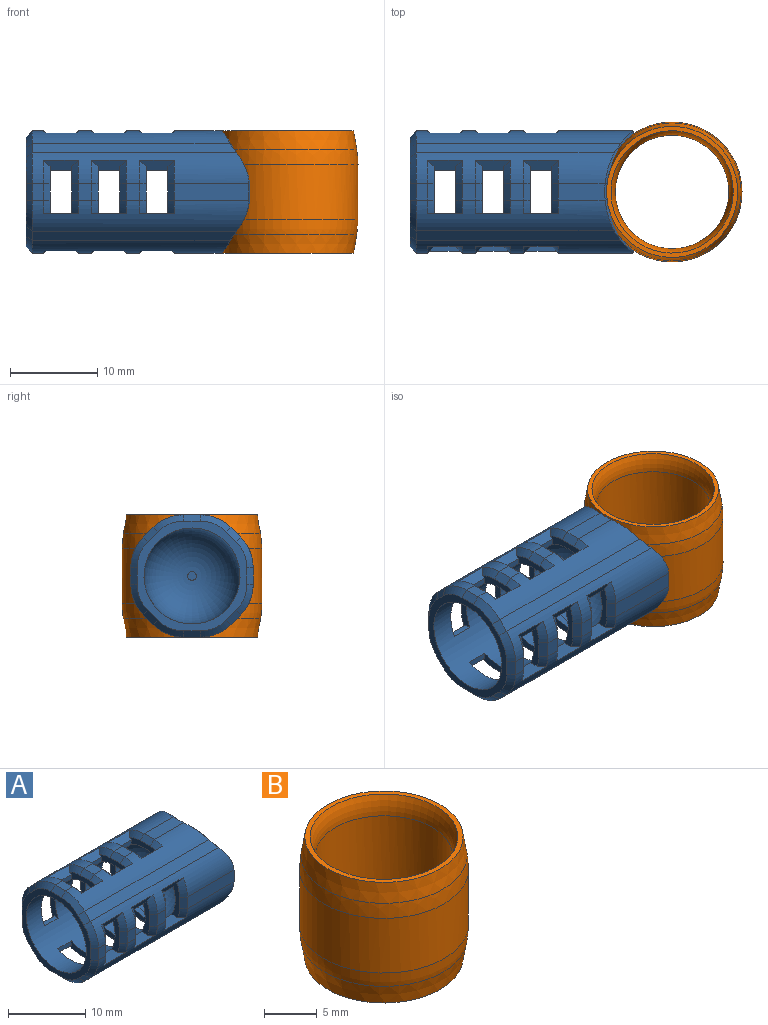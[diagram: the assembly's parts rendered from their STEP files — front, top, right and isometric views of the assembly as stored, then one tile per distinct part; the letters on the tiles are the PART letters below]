
ASSEMBLY  parts=2 mates=1
PART A: 197 faces, bbox 26x14x14 mm
  f0: plane 5.36x1.86mm, normal (0,0,-1), area 9.9mm2, adj f78,f79,f108,f190
  f1: plane 1.86x1.56mm, normal (0,0,-1), area 2.9mm2, adj f78,f79,f187,f194
  f2: plane 1.86x1.56mm, normal (0,0,-1), area 2.9mm2, adj f78,f79,f180,f183
  f3: plane 1.86x1.31mm, normal (0,-1,0), area 2.4mm2, adj f76,f77,f92,f113
  f4: plane 1.86x1.56mm, normal (0,-1,0), area 2.9mm2, adj f76,f77,f117,f120
  f5: plane 1.86x1.56mm, normal (0,-1,0), area 2.9mm2, adj f76,f77,f124,f127
  f6: plane 8.53x1.86mm, normal (0,1,0), area 15.8mm2, adj f74,f75,f100,f173
  f7: plane 1.86x1.56mm, normal (0,1,0), area 2.9mm2, adj f74,f75,f166,f169
  f8: plane 1.86x1.56mm, normal (0,1,0), area 2.9mm2, adj f74,f75,f159,f162
  f9: plane 1.86x1.31mm, normal (0,0,1), area 2.4mm2, adj f72,f73,f84,f134
  f10: plane 1.86x1.56mm, normal (0,0,1), area 2.9mm2, adj f72,f73,f138,f141
  f11: plane 1.86x1.56mm, normal (0,0,1), area 2.9mm2, adj f72,f73,f145,f152
  f12: cylinder r=5.5mm len=17mm, axis (-1,0,0), area 431.8mm2, adj f17,f20,f21,f22,f23,f24,f25,f26
  f13: plane 1.86x1.31mm, normal (0,1,0), area 2.4mm2, adj f74,f75,f83,f155
  f14: plane 8.53x1.86mm, normal (0,-1,0), area 15.8mm2, adj f76,f77,f107,f131
  f15: plane 5.36x1.86mm, normal (0,0,1), area 9.9mm2, adj f72,f73,f99,f148
  f16: plane 1.86x1.31mm, normal (0,0,-1), area 2.4mm2, adj f78,f79,f91,f176
  f17: plane 12.56x12.56mm, normal (-1,0,0), area 33.9mm2, adj f12,f80,f81,f82,f83,f84,f85,f86
  f18: cylinder r=7mm len=12.56mm, axis (0,0,1), area 125.1mm2, adj f96,f97,f98,f99,f100,f101,f102,f103
  f19: plane 1x1mm, normal (-1,0,0), area 0.8mm2, adj f196
  f20: plane 5.37x1.38mm, normal (1,0,0), area 4.6mm2, adj f12,f21,f23,f150,f151,f152,f153
  f21: plane 2.5x0.71mm, normal (0,-1,0), area 1.8mm2, adj f12,f20,f22,f150
  f22: plane 5.37x1.38mm, normal (-1,0,0), area 4.6mm2, adj f12,f21,f23,f147,f148,f149,f150
  f23: plane 3.97x1.87mm, normal (0,1,0), area 5.2mm2, adj f12,f20,f22,f72,f147,f153
  f24: plane 3.97x1.87mm, normal (0,1,0), area 5.2mm2, adj f12,f25,f27,f78,f189,f195
  f25: plane 5.37x1.38mm, normal (-1,0,0), area 4.6mm2, adj f12,f24,f26,f189,f190,f191,f192
  f26: plane 2.5x0.71mm, normal (0,-1,0), area 1.8mm2, adj f12,f25,f27,f192
  f27: plane 5.37x1.38mm, normal (1,0,0), area 4.6mm2, adj f12,f24,f26,f192,f193,f194,f195
  f28: plane 3.97x1.87mm, normal (0,0,1), area 5.2mm2, adj f12,f29,f31,f76,f126,f132
  f29: plane 5.37x1.38mm, normal (-1,0,0), area 4.6mm2, adj f12,f28,f30,f129,f130,f131,f132
  f30: plane 2.5x0.71mm, normal (0,0,-1), area 1.8mm2, adj f12,f29,f31,f129
  f31: plane 5.37x1.38mm, normal (1,0,0), area 4.6mm2, adj f12,f28,f30,f126,f127,f128,f129
  f32: plane 5.37x1.38mm, normal (1,0,0), area 4.6mm2, adj f12,f33,f35,f168,f169,f170,f171
  f33: plane 3.97x1.87mm, normal (0,0,-1), area 5.2mm2, adj f12,f32,f34,f75,f168,f174
  f34: plane 5.37x1.38mm, normal (-1,0,0), area 4.6mm2, adj f12,f33,f35,f171,f172,f173,f174
  f35: plane 2.5x0.71mm, normal (0,0,1), area 1.8mm2, adj f12,f32,f34,f171
  f36: plane 2.5x0.71mm, normal (0,-1,0), area 1.8mm2, adj f12,f37,f39,f178
  f37: plane 5.37x1.38mm, normal (-1,0,0), area 4.6mm2, adj f12,f36,f38,f178,f179,f180,f181
  f38: plane 3.97x1.87mm, normal (0,1,0), area 5.2mm2, adj f12,f37,f39,f78,f175,f181
  f39: plane 5.37x1.38mm, normal (1,0,0), area 4.6mm2, adj f12,f36,f38,f175,f176,f177,f178
  f40: plane 2.5x0.71mm, normal (0,-1,0), area 1.8mm2, adj f12,f41,f43,f185
  f41: plane 5.37x1.38mm, normal (-1,0,0), area 4.6mm2, adj f12,f40,f42,f185,f186,f187,f188
  f42: plane 3.97x1.87mm, normal (0,1,0), area 5.2mm2, adj f12,f41,f43,f78,f182,f188
  f43: plane 5.37x1.38mm, normal (1,0,0), area 4.6mm2, adj f12,f40,f42,f182,f183,f184,f185
  f44: plane 5.37x1.38mm, normal (1,0,0), area 4.6mm2, adj f12,f45,f47,f133,f134,f135,f136
  f45: plane 3.97x1.87mm, normal (0,1,0), area 5.2mm2, adj f12,f44,f46,f72,f133,f139
  f46: plane 5.37x1.38mm, normal (-1,0,0), area 4.6mm2, adj f12,f45,f47,f136,f137,f138,f139
  f47: plane 2.5x0.71mm, normal (0,-1,0), area 1.8mm2, adj f12,f44,f46,f136
  f48: plane 5.37x1.38mm, normal (1,0,0), area 4.6mm2, adj f12,f49,f51,f140,f141,f142,f143
  f49: plane 3.97x1.87mm, normal (0,1,0), area 5.2mm2, adj f12,f48,f50,f72,f140,f146
  f50: plane 5.37x1.38mm, normal (-1,0,0), area 4.6mm2, adj f12,f49,f51,f143,f144,f145,f146
  f51: plane 2.5x0.71mm, normal (0,-1,0), area 1.8mm2, adj f12,f48,f50,f143
  f52: plane 3.97x1.87mm, normal (0,0,1), area 5.2mm2, adj f12,f53,f55,f76,f119,f125
  f53: plane 5.37x1.38mm, normal (-1,0,0), area 4.6mm2, adj f12,f52,f54,f122,f123,f124,f125
  f54: plane 2.5x0.71mm, normal (0,0,-1), area 1.8mm2, adj f12,f53,f55,f122
  f55: plane 5.37x1.38mm, normal (1,0,0), area 4.6mm2, adj f12,f52,f54,f119,f120,f121,f122
  f56: plane 3.97x1.87mm, normal (0,0,1), area 5.2mm2, adj f12,f57,f59,f76,f112,f118
  f57: plane 5.37x1.38mm, normal (-1,0,0), area 4.6mm2, adj f12,f56,f58,f115,f116,f117,f118
  f58: plane 2.5x0.71mm, normal (0,0,-1), area 1.8mm2, adj f12,f57,f59,f115
  f59: plane 5.37x1.38mm, normal (1,0,0), area 4.6mm2, adj f12,f56,f58,f112,f113,f114,f115
  f60: plane 5.37x1.38mm, normal (1,0,0), area 4.6mm2, adj f12,f61,f63,f161,f162,f163,f164
  f61: plane 3.97x1.87mm, normal (0,0,-1), area 5.2mm2, adj f12,f60,f62,f75,f161,f167
  f62: plane 5.37x1.38mm, normal (-1,0,0), area 4.6mm2, adj f12,f61,f63,f164,f165,f166,f167
  f63: plane 2.5x0.71mm, normal (0,0,1), area 1.8mm2, adj f12,f60,f62,f164
  f64: plane 5.37x1.38mm, normal (1,0,0), area 4.6mm2, adj f12,f65,f67,f154,f155,f156,f157
  f65: plane 3.97x1.87mm, normal (0,0,-1), area 5.2mm2, adj f12,f64,f66,f75,f154,f160
  f66: plane 5.37x1.38mm, normal (-1,0,0), area 4.6mm2, adj f12,f65,f67,f157,f158,f159,f160
  f67: plane 2.5x0.71mm, normal (0,0,1), area 1.8mm2, adj f12,f64,f66,f157
  f68: plane 23.41x1.07mm, normal (0,-0.71,-0.71), area 34.8mm2, adj f76,f78,f95,f111
  f69: plane 23.41x1.07mm, normal (0,0.71,-0.71), area 34.8mm2, adj f74,f79,f87,f104
  f70: plane 23.41x1.07mm, normal (0,-0.71,0.71), area 34.8mm2, adj f72,f77,f88,f103
  f71: plane 23.41x1.07mm, normal (0,0.71,0.71), area 34.8mm2, adj f73,f75,f80,f96
  f72: cylinder r=5mm len=22.64mm, axis (-1,0,0), area 68mm2, adj f9,f10,f11,f15,f23,f45,f49,f70
  f73: cylinder r=5mm len=22.64mm, axis (-1,0,0), area 53.4mm2, adj f9,f10,f11,f15,f71,f82,f97,f135
  f74: cylinder r=5mm len=24.78mm, axis (-1,0,0), area 61.1mm2, adj f6,f7,f8,f13,f69,f85,f102,f156
  f75: cylinder r=5mm len=24.78mm, axis (-1,0,0), area 75.7mm2, adj f6,f7,f8,f13,f33,f61,f65,f71
  f76: cylinder r=5mm len=24.78mm, axis (1,0,0), area 75.7mm2, adj f3,f4,f5,f14,f28,f52,f56,f68
  f77: cylinder r=5mm len=24.78mm, axis (1,0,0), area 61.1mm2, adj f3,f4,f5,f14,f70,f90,f105,f114
  f78: cylinder r=5mm len=22.64mm, axis (1,0,0), area 68mm2, adj f0,f1,f2,f16,f24,f38,f42,f68
  f79: cylinder r=5mm len=22.64mm, axis (1,0,0), area 53.4mm2, adj f0,f1,f2,f16,f69,f89,f106,f177
  f80: plane 1.58x1.58mm, normal (-0.71,0.5,0.5), area 1.5mm2, adj f17,f71,f81,f82
  f81: cone r=4.28mm half-angle=45deg, axis (1,0,0), area 3.7mm2, adj f17,f75,f80,f83
  f82: cone r=4.28mm half-angle=45deg, axis (1,0,0), area 3.7mm2, adj f17,f73,f80,f84
  f83: plane 1.86x0.72mm, normal (-0.71,0.71,0), area 1.9mm2, adj f13,f17,f81,f85
  f84: plane 1.86x0.72mm, normal (-0.71,0,0.71), area 1.9mm2, adj f9,f17,f82,f86
  f85: cone r=4.28mm half-angle=45deg, axis (1,0,0), area 3.7mm2, adj f17,f74,f83,f87
  f86: cone r=4.28mm half-angle=45deg, axis (1,0,0), area 3.7mm2, adj f17,f72,f84,f88
  f87: plane 1.58x1.58mm, normal (-0.71,0.5,-0.5), area 1.5mm2, adj f17,f69,f85,f89
  f88: plane 1.58x1.58mm, normal (-0.71,-0.5,0.5), area 1.5mm2, adj f17,f70,f86,f90
  f89: cone r=4.28mm half-angle=45deg, axis (1,0,0), area 3.7mm2, adj f17,f79,f87,f91
  f90: cone r=4.28mm half-angle=45deg, axis (1,0,0), area 3.7mm2, adj f17,f77,f88,f92
  f91: plane 1.86x0.72mm, normal (-0.71,0,-0.71), area 1.9mm2, adj f16,f17,f89,f93
  f92: plane 1.86x0.72mm, normal (-0.71,-0.71,0), area 1.9mm2, adj f3,f17,f90,f94
  f93: cone r=4.28mm half-angle=45deg, axis (1,0,0), area 3.7mm2, adj f17,f78,f91,f95
  f94: cone r=4.28mm half-angle=45deg, axis (1,0,0), area 3.7mm2, adj f17,f76,f92,f95
  f95: plane 1.58x1.58mm, normal (-0.71,-0.5,-0.5), area 1.5mm2, adj f17,f68,f93,f94
  f96: bspline ~1.95x1.58mm, area 2mm2, adj f18,f71,f97,f98
  f97: bspline ~3.62x1.98mm, area 4mm2, adj f18,f73,f96,f99
  f98: bspline ~3.54x2.45mm, area 5.1mm2, adj f18,f75,f96,f100
  f99: cone r=7mm half-angle=45deg, axis (0,0,1), area 1.8mm2, adj f15,f18,f97,f101
  f100: plane 1.86x1.31mm, normal (0.95,0.31,0), area 2.6mm2, adj f6,f18,f98,f102
  f101: bspline ~3.62x1.98mm, area 4mm2, adj f18,f72,f99,f103
  f102: bspline ~3.54x2.45mm, area 5.1mm2, adj f18,f74,f100,f104
  f103: bspline ~1.95x1.58mm, area 2mm2, adj f18,f70,f101,f105
  f104: bspline ~1.95x1.58mm, area 2mm2, adj f18,f69,f102,f106
  f105: bspline ~3.54x2.45mm, area 5.1mm2, adj f18,f77,f103,f107
  f106: bspline ~3.62x1.98mm, area 4mm2, adj f18,f79,f104,f108
  f107: plane 1.86x1.31mm, normal (0.95,-0.31,0), area 2.6mm2, adj f14,f18,f105,f109
  f108: cone r=7.72mm half-angle=45deg, axis (0,0,-1), area 1.8mm2, adj f0,f18,f106,f110
  f109: bspline ~3.54x2.45mm, area 5.1mm2, adj f18,f76,f107,f111
  f110: bspline ~3.62x1.98mm, area 4mm2, adj f18,f78,f108,f111
  f111: bspline ~1.95x1.58mm, area 2mm2, adj f18,f68,f109,f110
  f112: cone r=4.28mm half-angle=45deg, axis (-1,0,0), area 1.6mm2, adj f56,f59,f76,f113
  f113: plane 1.86x0.72mm, normal (0.71,-0.71,0), area 1.9mm2, adj f3,f59,f112,f114
  f114: cone r=4.28mm half-angle=45deg, axis (-1,0,0), area 2.5mm2, adj f59,f77,f113,f115
  f115: plane 3.98x1.15mm, normal (0,-0.88,-0.48), area 3.8mm2, adj f57,f58,f59,f77,f114,f116
  f116: cone r=4.28mm half-angle=45deg, axis (1,0,0), area 2.5mm2, adj f57,f77,f115,f117
  f117: plane 1.86x0.72mm, normal (-0.71,-0.71,0), area 1.9mm2, adj f4,f57,f116,f118
  f118: cone r=4.28mm half-angle=45deg, axis (1,0,0), area 1.6mm2, adj f56,f57,f76,f117
  f119: cone r=4.28mm half-angle=45deg, axis (-1,0,0), area 1.6mm2, adj f52,f55,f76,f120
  f120: plane 1.86x0.72mm, normal (0.71,-0.71,0), area 1.9mm2, adj f4,f55,f119,f121
  f121: cone r=4.28mm half-angle=45deg, axis (-1,0,0), area 2.5mm2, adj f55,f77,f120,f122
  f122: plane 3.98x1.15mm, normal (0,-0.88,-0.48), area 3.8mm2, adj f53,f54,f55,f77,f121,f123
  f123: cone r=4.28mm half-angle=45deg, axis (1,0,0), area 2.5mm2, adj f53,f77,f122,f124
  f124: plane 1.86x0.72mm, normal (-0.71,-0.71,0), area 1.9mm2, adj f5,f53,f123,f125
  f125: cone r=4.28mm half-angle=45deg, axis (1,0,0), area 1.6mm2, adj f52,f53,f76,f124
  f126: cone r=4.28mm half-angle=45deg, axis (-1,0,0), area 1.6mm2, adj f28,f31,f76,f127
  f127: plane 1.86x0.72mm, normal (0.71,-0.71,0), area 1.9mm2, adj f5,f31,f126,f128
  f128: cone r=4.28mm half-angle=45deg, axis (-1,0,0), area 2.5mm2, adj f31,f77,f127,f129
  f129: plane 3.98x1.15mm, normal (0,-0.88,-0.48), area 3.8mm2, adj f29,f30,f31,f77,f128,f130
  f130: cone r=4.28mm half-angle=45deg, axis (1,0,0), area 2.5mm2, adj f29,f77,f129,f131
  f131: plane 1.86x0.72mm, normal (-0.71,-0.71,0), area 1.9mm2, adj f14,f29,f130,f132
  f132: cone r=4.28mm half-angle=45deg, axis (1,0,0), area 1.6mm2, adj f28,f29,f76,f131
  f133: cone r=4.28mm half-angle=45deg, axis (-1,0,0), area 1.6mm2, adj f44,f45,f72,f134
  f134: plane 1.86x0.72mm, normal (0.71,0,0.71), area 1.9mm2, adj f9,f44,f133,f135
  f135: cone r=4.28mm half-angle=45deg, axis (-1,0,0), area 2.5mm2, adj f44,f73,f134,f136
  f136: plane 3.98x1.15mm, normal (0,-0.48,0.88), area 3.8mm2, adj f44,f46,f47,f73,f135,f137
  f137: cone r=4.28mm half-angle=45deg, axis (1,0,0), area 2.5mm2, adj f46,f73,f136,f138
  f138: plane 1.86x0.72mm, normal (-0.71,0,0.71), area 1.9mm2, adj f10,f46,f137,f139
  f139: cone r=4.28mm half-angle=45deg, axis (1,0,0), area 1.6mm2, adj f45,f46,f72,f138
  f140: cone r=4.28mm half-angle=45deg, axis (-1,0,0), area 1.6mm2, adj f48,f49,f72,f141
  f141: plane 1.86x0.72mm, normal (0.71,0,0.71), area 1.9mm2, adj f10,f48,f140,f142
  f142: cone r=4.28mm half-angle=45deg, axis (-1,0,0), area 2.5mm2, adj f48,f73,f141,f143
  f143: plane 3.98x1.15mm, normal (0,-0.48,0.88), area 3.8mm2, adj f48,f50,f51,f73,f142,f144
  f144: cone r=4.28mm half-angle=45deg, axis (1,0,0), area 2.5mm2, adj f50,f73,f143,f145
  f145: plane 1.86x0.72mm, normal (-0.71,0,0.71), area 1.9mm2, adj f11,f50,f144,f146
  f146: cone r=4.28mm half-angle=45deg, axis (1,0,0), area 1.6mm2, adj f49,f50,f72,f145
  f147: cone r=4.28mm half-angle=45deg, axis (1,0,0), area 1.6mm2, adj f22,f23,f72,f148
  f148: plane 1.86x0.72mm, normal (-0.71,0,0.71), area 1.9mm2, adj f15,f22,f147,f149
  f149: cone r=4.28mm half-angle=45deg, axis (1,0,0), area 2.5mm2, adj f22,f73,f148,f150
  f150: plane 3.98x1.15mm, normal (0,-0.48,0.88), area 3.8mm2, adj f20,f21,f22,f73,f149,f151
  f151: cone r=4.28mm half-angle=45deg, axis (-1,0,0), area 2.5mm2, adj f20,f73,f150,f152
  f152: plane 1.86x0.72mm, normal (0.71,0,0.71), area 1.9mm2, adj f11,f20,f151,f153
  f153: cone r=4.28mm half-angle=45deg, axis (-1,0,0), area 1.6mm2, adj f20,f23,f72,f152
  f154: cone r=4.28mm half-angle=45deg, axis (-1,0,0), area 1.6mm2, adj f64,f65,f75,f155
  f155: plane 1.86x0.72mm, normal (0.71,0.71,0), area 1.9mm2, adj f13,f64,f154,f156
  f156: cone r=4.28mm half-angle=45deg, axis (-1,0,0), area 2.5mm2, adj f64,f74,f155,f157
  f157: plane 3.98x1.15mm, normal (0,0.88,0.48), area 3.8mm2, adj f64,f66,f67,f74,f156,f158
  f158: cone r=4.28mm half-angle=45deg, axis (1,0,0), area 2.5mm2, adj f66,f74,f157,f159
  f159: plane 1.86x0.72mm, normal (-0.71,0.71,0), area 1.9mm2, adj f8,f66,f158,f160
  f160: cone r=4.28mm half-angle=45deg, axis (1,0,0), area 1.6mm2, adj f65,f66,f75,f159
  f161: cone r=4.28mm half-angle=45deg, axis (-1,0,0), area 1.6mm2, adj f60,f61,f75,f162
  f162: plane 1.86x0.72mm, normal (0.71,0.71,0), area 1.9mm2, adj f8,f60,f161,f163
  f163: cone r=4.28mm half-angle=45deg, axis (-1,0,0), area 2.5mm2, adj f60,f74,f162,f164
  f164: plane 3.98x1.15mm, normal (0,0.88,0.48), area 3.8mm2, adj f60,f62,f63,f74,f163,f165
  f165: cone r=4.28mm half-angle=45deg, axis (1,0,0), area 2.5mm2, adj f62,f74,f164,f166
  f166: plane 1.86x0.72mm, normal (-0.71,0.71,0), area 1.9mm2, adj f7,f62,f165,f167
  f167: cone r=4.28mm half-angle=45deg, axis (1,0,0), area 1.6mm2, adj f61,f62,f75,f166
  f168: cone r=4.28mm half-angle=45deg, axis (-1,0,0), area 1.6mm2, adj f32,f33,f75,f169
  f169: plane 1.86x0.72mm, normal (0.71,0.71,0), area 1.9mm2, adj f7,f32,f168,f170
  f170: cone r=4.28mm half-angle=45deg, axis (-1,0,0), area 2.5mm2, adj f32,f74,f169,f171
  f171: plane 3.98x1.15mm, normal (0,0.88,0.48), area 3.8mm2, adj f32,f34,f35,f74,f170,f172
  f172: cone r=4.28mm half-angle=45deg, axis (1,0,0), area 2.5mm2, adj f34,f74,f171,f173
  f173: plane 1.86x0.72mm, normal (-0.71,0.71,0), area 1.9mm2, adj f6,f34,f172,f174
  f174: cone r=4.28mm half-angle=45deg, axis (1,0,0), area 1.6mm2, adj f33,f34,f75,f173
  f175: cone r=4.28mm half-angle=45deg, axis (-1,0,0), area 1.6mm2, adj f38,f39,f78,f176
  f176: plane 1.86x0.72mm, normal (0.71,0,-0.71), area 1.9mm2, adj f16,f39,f175,f177
  f177: cone r=4.28mm half-angle=45deg, axis (-1,0,0), area 2.5mm2, adj f39,f79,f176,f178
  f178: plane 3.98x1.15mm, normal (0,-0.48,-0.88), area 3.8mm2, adj f36,f37,f39,f79,f177,f179
  f179: cone r=4.28mm half-angle=45deg, axis (1,0,0), area 2.5mm2, adj f37,f79,f178,f180
  f180: plane 1.86x0.72mm, normal (-0.71,0,-0.71), area 1.9mm2, adj f2,f37,f179,f181
  f181: cone r=4.28mm half-angle=45deg, axis (1,0,0), area 1.6mm2, adj f37,f38,f78,f180
  f182: cone r=4.28mm half-angle=45deg, axis (-1,0,0), area 1.6mm2, adj f42,f43,f78,f183
  f183: plane 1.86x0.72mm, normal (0.71,0,-0.71), area 1.9mm2, adj f2,f43,f182,f184
  f184: cone r=4.28mm half-angle=45deg, axis (-1,0,0), area 2.5mm2, adj f43,f79,f183,f185
  f185: plane 3.98x1.15mm, normal (0,-0.48,-0.88), area 3.8mm2, adj f40,f41,f43,f79,f184,f186
  f186: cone r=4.28mm half-angle=45deg, axis (1,0,0), area 2.5mm2, adj f41,f79,f185,f187
  f187: plane 1.86x0.72mm, normal (-0.71,0,-0.71), area 1.9mm2, adj f1,f41,f186,f188
  f188: cone r=4.28mm half-angle=45deg, axis (1,0,0), area 1.6mm2, adj f41,f42,f78,f187
  f189: cone r=4.28mm half-angle=45deg, axis (1,0,0), area 1.6mm2, adj f24,f25,f78,f190
  f190: plane 1.86x0.72mm, normal (-0.71,0,-0.71), area 1.9mm2, adj f0,f25,f189,f191
  f191: cone r=4.28mm half-angle=45deg, axis (1,0,0), area 2.5mm2, adj f25,f79,f190,f192
  f192: plane 3.98x1.15mm, normal (0,-0.48,-0.88), area 3.8mm2, adj f25,f26,f27,f79,f191,f193
  f193: cone r=4.28mm half-angle=45deg, axis (-1,0,0), area 2.5mm2, adj f27,f79,f192,f194
  f194: plane 1.86x0.72mm, normal (0.71,0,-0.71), area 1.9mm2, adj f1,f27,f193,f195
  f195: cone r=4.28mm half-angle=45deg, axis (-1,0,0), area 1.6mm2, adj f24,f27,f78,f194
  f196: torus R=0.5mm, axis (-1,0,0), area 181.8mm2, adj f12,f19
PART B: 10 faces, bbox 17.2x17.2x16.7 mm
  f0: cylinder r=6.5mm len=13mm, axis (0,0,-1), area 393.7mm2, adj f8,f9
  f1: cylinder r=8mm len=16mm, axis (0,0,-1), area 318.9mm2, adj f6,f7
  f2: plane 15x15mm, normal (0,0,1), area 22.8mm2, adj f5,f8
  f3: plane 15x15mm, normal (0,0,-1), area 22.8mm2, adj f4,f9
  f4: cone r=8mm half-angle=9.5deg, axis (0,0,1), area 106.9mm2, adj f3,f6
  f5: cone r=7.5mm half-angle=9.5deg, axis (0,0,-1), area 106.9mm2, adj f2,f7
  f6: revolved ~16x16mm, area 165.1mm2, adj f1,f4
  f7: revolved ~16x16mm, area 165.1mm2, adj f1,f5
  f8: torus R=11.5mm, axis (0,0,1), area 94.5mm2, adj f0,f2
  f9: torus R=11.5mm, axis (0,0,-1), area 94.5mm2, adj f0,f3
PLACE A t=(-15,0,0)mm
PLACE B at identity
MATE fastened A.f18 <-> B.f0  axis (0,0,1) through (0,0,7)mm
